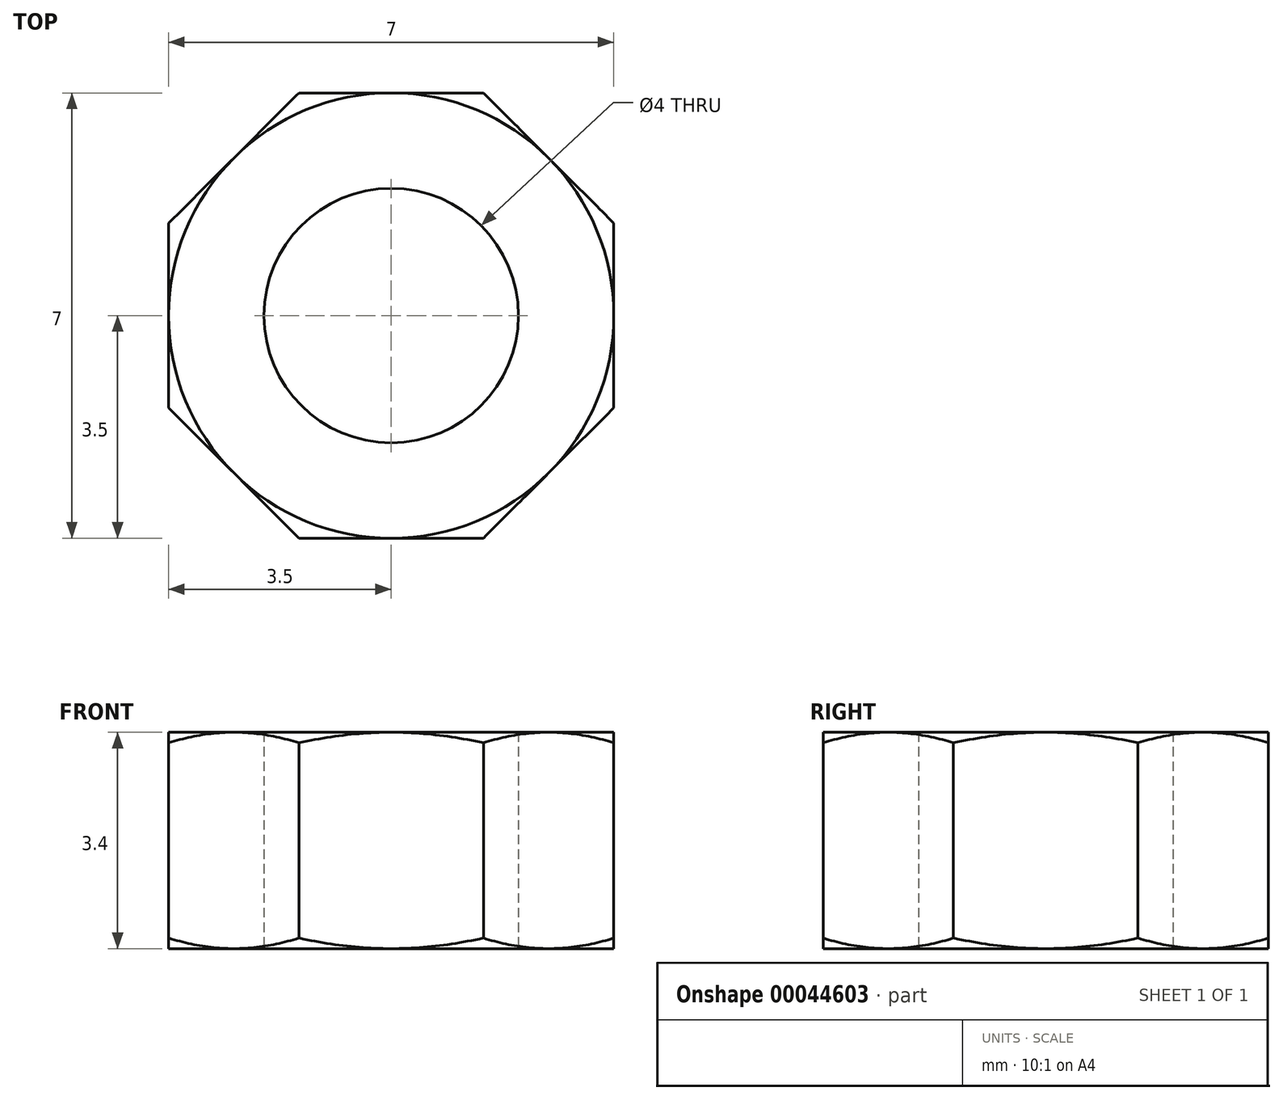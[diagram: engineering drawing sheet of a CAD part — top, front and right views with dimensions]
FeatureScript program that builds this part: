
annotation { "Feature Type Name" : "Feature", "Feature Type Description" : "" }
export const myFeature = defineFeature(function(context is Context, id is Id, definition is map)
    precondition{}
    {
        {
            var Q0;
            Q0=qCreatedBy(makeId("Top.planeOp"),FACE);
            var sketch = newSketch(context, id + "F0", { "sketchPlane" : qUnion([Q0])});
            skCircle(sketch, "E0.cCircle", {"center": v(0, 0) * mm, "radius": 3.5 * mm, "construction": true});
            skLineSegment(sketch, "E0.0", {"start": v(3.5, -1.45) * mm, "end": v(1.45, -3.5) * mm});
            skLineSegment(sketch, "E0.1", {"start": v(1.45, -3.5) * mm, "end": v(-1.45, -3.5) * mm});
            skLineSegment(sketch, "E0.2", {"start": v(-1.45, -3.5) * mm, "end": v(-3.5, -1.45) * mm});
            skLineSegment(sketch, "E0.3", {"start": v(-3.5, -1.45) * mm, "end": v(-3.5, 1.45) * mm});
            skLineSegment(sketch, "E0.4", {"start": v(-3.5, 1.45) * mm, "end": v(-1.45, 3.5) * mm});
            skLineSegment(sketch, "E0.5", {"start": v(-1.45, 3.5) * mm, "end": v(1.45, 3.5) * mm});
            skLineSegment(sketch, "E0.6", {"start": v(1.45, 3.5) * mm, "end": v(3.5, 1.45) * mm});
            skLineSegment(sketch, "E0.7", {"start": v(3.5, 1.45) * mm, "end": v(3.5, -1.45) * mm});
            skPoint(sketch, "E0.0.midPoint", {"position": v(2.47, -2.47) * mm});
            skCircle(sketch, "E1", {"center": v(0, 0) * mm, "radius": 2 * mm});
            skSolve(sketch);
        }
        {
            var Q0;
            Q0=makeQuery(id+"F0.imprint","IMPRINT",FACE,{"disambiguationData":[TD([[makeQuery(id+"F0.imprint","IMPRINT",EDGE,{"derivedFrom":sQuery(id+"F0.wireOp",EDGE,"E0.0")}),-1.0]])]});
            extrude(context, id + "F1", {"entities" : qUnion([Q0]), "depth" : 3.4 * mm});
        }
        {
            var Q0;
            Q0=qCreatedBy(makeId("Front.planeOp"),FACE);
            var sketch = newSketch(context, id + "F2", { "sketchPlane" : qUnion([Q0])});
            skLineSegment(sketch, "E2", {"start": v(0, 0) * mm, "end": v(0, 3.4) * mm, "construction": true});
            skLineSegment(sketch, "E3", {"start": v(0, 3.4) * mm, "end": v(0, 1.7) * mm, "construction": true});
            skLineSegment(sketch, "E4", {"start": v(0, 1.7) * mm, "end": v(-3.5, 1.7) * mm, "construction": true});
            skLineSegment(sketch, "E5", {"start": v(-3.5, 3.4) * mm, "end": v(-5.13, 3.4) * mm});
            skLineSegment(sketch, "E6", {"start": v(-5.13, 2.46) * mm, "end": v(-5.13, 3.4) * mm});
            skLineSegment(sketch, "E7", {"start": v(-5.13, 2.46) * mm, "end": v(-3.5, 3.4) * mm});
            skLineSegment(sketch, "E8.MirrorCS", {"start": v(-5.13, 0.94) * mm, "end": v(-3.5, 0) * mm});
            skLineSegment(sketch, "E9.MirrorCS", {"start": v(-3.5, 0) * mm, "end": v(-5.13, 0) * mm});
            skLineSegment(sketch, "E10.MirrorCS", {"start": v(-5.13, 0.94) * mm, "end": v(-5.13, 0) * mm});
            skSolve(sketch);
        }
        {
            var Q0;
            Q0 = qSketchRegion(id + "F2", true);
            var Q1;
            Q1=sQuery(id+"F2.wireOp",EDGE,"E2");
            revolve(context, id + "F3", {"operationType" : NewBodyOperationType.REMOVE, "entities" : qUnion([Q0]), "axis" : qUnion([Q1]), "revolveType" : RevolveType.FULL, "oppositeDirection" : true});
        }
    });
